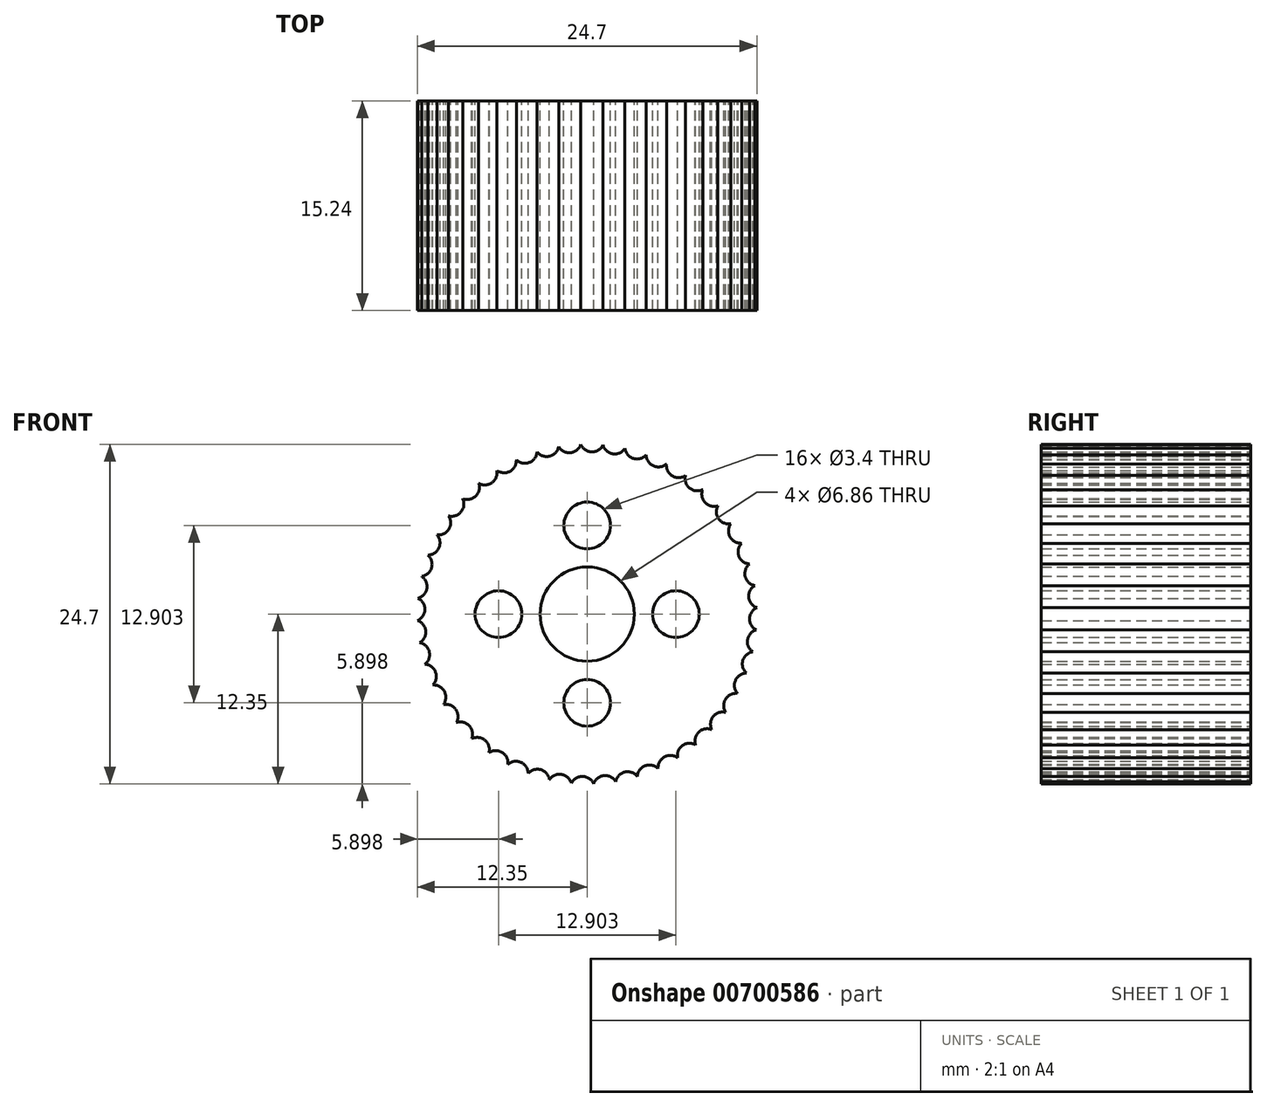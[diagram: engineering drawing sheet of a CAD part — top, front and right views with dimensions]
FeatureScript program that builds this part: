
annotation { "Feature Type Name" : "Feature", "Feature Type Description" : "" }
export const myFeature = defineFeature(function(context is Context, id is Id, definition is map)
    precondition{}
    {
        {
            var Q0;
            Q0=qCreatedBy(makeId("Front.planeOp"),FACE);
            var sketch = newSketch(context, id + "F0", { "sketchPlane" : qUnion([Q0])});
            skCircle(sketch, "E0", {"center": v(0, 0) * mm, "radius": 3.43 * mm});
            skCircle(sketch, "E1", {"center": v(0, 6.45) * mm, "radius": 1.7 * mm});
            skCircle(sketch, "E2", {"center": v(6.45, 0) * mm, "radius": 1.7 * mm});
            skCircle(sketch, "E3", {"center": v(0, -6.45) * mm, "radius": 1.7 * mm});
            skCircle(sketch, "E4", {"center": v(-6.45, 0) * mm, "radius": 1.7 * mm});
            skCircle(sketch, "E5", {"center": v(0, 0) * mm, "radius": 12.7 * mm});
            skSolve(sketch);
        }
        {
            var Q0;
            Q0 = qSketchRegion(id + "F0", true);
            extrude(context, id + "F1", {"entities" : qUnion([Q0]), "depth" : 15.24 * mm, "offsetDistance" : 25.4 * mm});
        }
        {
            var Q0;
            Q0=qCreatedBy(makeId("Right.planeOp"),FACE);
            var sketch = newSketch(context, id + "F2", { "sketchPlane" : qUnion([Q0])});
            skLineSegment(sketch, "E6", {"start": v(24.8, 0) * mm, "end": v(-23.69, 0) * mm});
            skSolve(sketch);
        }
        {
            var Q0;
            Q0=makeQuery(id+"F1.opExtrude","CAP_FACE",FACE,{"disambiguationData":[OSD([sQuery(id+"F0.wireOp",EDGE,"E0"),sQuery(id+"F0.wireOp",EDGE,"E1"),sQuery(id+"F0.wireOp",EDGE,"E2"),sQuery(id+"F0.wireOp",EDGE,"E3"),sQuery(id+"F0.wireOp",EDGE,"E4"),sQuery(id+"F0.wireOp",EDGE,"E5")])],"isStart":false});
            var sketch = newSketch(context, id + "F3", { "sketchPlane" : qUnion([Q0])});
            skCircle(sketch, "E7", {"center": v(-7.45, 10.29) * mm, "radius": 0.89 * mm});
            skSolve(sketch);
        }
        {
            var Q0;
            Q0 = qSketchRegion(id + "F3", true);
            extrude(context, id + "F4", {"entities" : qUnion([Q0]), "endBound" : BoundingType.SYMMETRIC, "depth" : 50.8 * mm, "offsetDistance" : 25.4 * mm});
        }
        {
            var Q0;
            Q0=makeQuery(id+"F4.opExtrude","SWEPT_BODY",BODY,{"disambiguationData":[OSD([sQuery(id+"F3.wireOp",EDGE,"E7")])]});
            var Q1;
            Q1=sQuery(id+"F2.wireOp",EDGE,"E6");
            circularPattern(context, id + "F5", {"operationType" : NewBodyOperationType.REMOVE, "entities" : qUnion([Q0]), "axis" : qUnion([Q1]), "angle" : 360 * degree, "instanceCount" : 48, "equalSpace" : true});
        }
    });
